# Revit family: Sink-Wall_Mount-KOHLER-Kingston-K-2007
name_source: partatom
category: Plumbing Fixtures
revit_build: Autodesk Revit 2015 (Build: 20140606_1530(x64)
units: mm (PartAtom-declared; Revit-internal decimal feet)

## types (6) — shared parameters
ADA Compliant = Yes
Assembly Code = D2010400
CW Connection = No
Cold Water Inlet = Cold Water Inlet
Date Modified = 08/23/2018
Default Elevation = 34"
Drain Included = No
Environmental Product Declaration = https://www.us.kohler.com
HW Connection = No
Height = 12 1/4"
Hot Water Inlet = Hot Water Inlet
Length = 21 1/4"
Manufacturer = KOHLER Co.
MasterFormat 1995 = 15410
MasterFormat 2004 = 22.41.16
Material = Vitreous china
Product Documentation Link = http://www.us.kohler.com
Product Name = Kingston
Product Page URL = http://www.us.kohler.com
URL = https://www.us.kohler.com
Vent Connection = No
Waste Connection = Yes
Waste Water Outlet = Waste Water Outlet
Width = 18 1/8"

## per-type parameters (varying)
| type | Description | Finish | Model | Type | _L | _R |
| 0-White | 21 1/4Inch x 18 1/8Inch wall-mount/concealed arm carrier bathroom sink with single faucet hole | Kohler-Vitreous_China-0-White | K-2007-0 | 1 | No | No |
| 47-Almond | 21 1/4Inch x 18 1/8Inch wall-mount/concealed arm carrier bathroom sink with single faucet hole | Kohler-Vitreous_China-47-Almond | K-2007-47 | 2 | No | No |
| Left Soap Dispenser, 0-White | 21 1/4Inch x 18 1/8Inch wall-mount/concealed arm carrier bathroom sink with single faucet hole and left-hand soap dispenser hole | Kohler-Vitreous_China-0-White | K-2007-L-0 | 3 | Yes | No |
| Left Soap Dispenser, 47-Almond | 21 1/4Inch x 18 1/8Inch wall-mount/concealed arm carrier bathroom sink with single faucet hole and left-hand soap dispenser hole | Kohler-Vitreous_China-47-Almond | K-2007-L-47 | 4 | Yes | No |
| Right Soap Dispenser, 0-White | 21 1/4Inch x 18 1/8Inch wall-mount/concealed arm carrier bathroom sink with single faucet hole and right-hand soap dispenser hole | Kohler-Vitreous_China-0-White | K-2007-R-0 | 5 | No | Yes |
| Right Soap Dispenser, 47-Almond | 21 1/4Inch x 18 1/8Inch wall-mount/concealed arm carrier bathroom sink with single faucet hole and right-hand soap dispenser hole | Kohler-Vitreous_China-47-Almond | K-2007-R-47 | 6 | No | Yes |

## geometry (parser evidence)
native form markers: Sweep x5
no freeform markers — native parametric forms only
